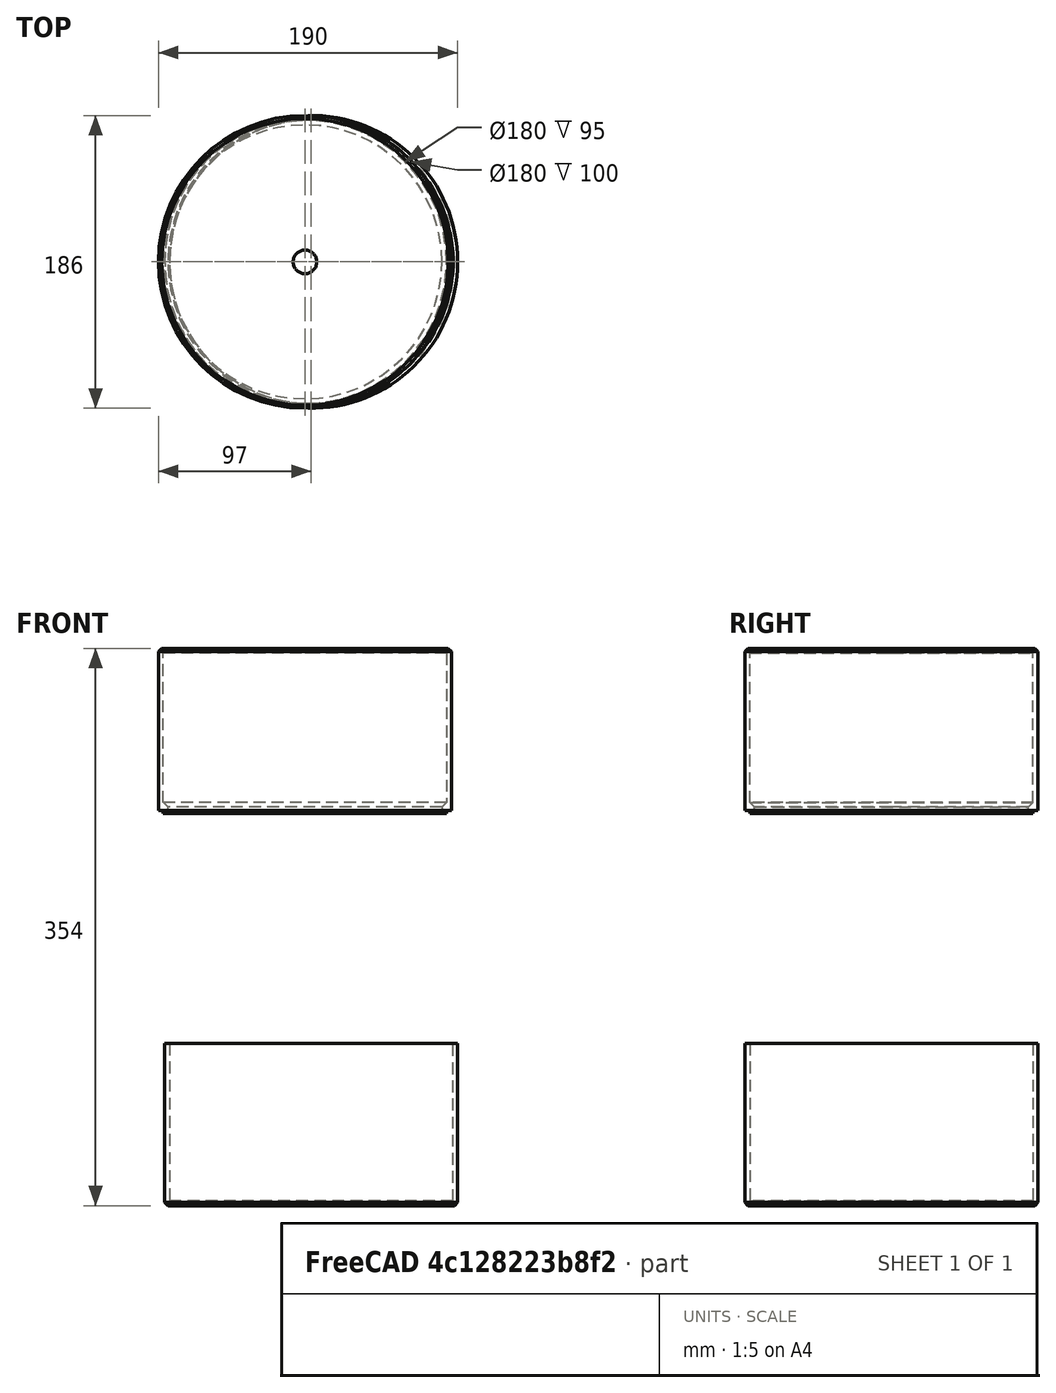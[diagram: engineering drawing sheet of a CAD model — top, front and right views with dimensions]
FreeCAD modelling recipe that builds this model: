
FCSTD DOCUMENT  (FreeCAD 1.0R39285 (Git))
Label: CanHalves
License: All rights reserved
LicenseURL: http://en.wikipedia.org/wiki/All_rights_reserved
objects: PartDesign::Chamfer×3, App::Link×2, App::FeaturePython×2, Sketcher::SketchObject×2, PartDesign::Body×2, PartDesign::AdditiveCylinder×1, PartDesign::Thickness×1, PartDesign::FeatureBase×1, PartDesign::Pad×1, Assembly::JointGroup×1, Assembly::AssemblyObject×1, PartDesign::Pocket×1
note: 29 computed .brp shape members not serialized (recipe doc carries the construction recipe); baked Part::Feature solids carry a one-line shape summary decoded from their .brp

FEATURE [PartDesign::AdditiveCylinder] Cylinder
  Angle = 360
  AttacherType = Attacher::AttachEngine3D
  Dimensions_Diameter = 180
  Dimensions_Height = 200
  Dimensions_Thickness = 3
  FirstAngle = 0
  Height = 103
  Radius = 93
  SecondAngle = 0
  Suppressed = false
  expr: Height = Dimensions_Height / 2 + Dimensions_Thickness
  expr: Radius = Dimensions_Diameter / 2 + Dimensions_Thickness
FEATURE [PartDesign::Thickness] Thickness
  Base = -> Cylinder [Face3]
  BaseFeature = -> Cylinder
  Intersection = false
  Join = 0
  Mode = 0
  Reversed = true
  SupportTransform = false
  Suppressed = false
  Value = 3
  expr: Value = <<Cylinder>>.Dimensions_Thickness
FEATURE [PartDesign::FeatureBase] Clone
  BaseFeature = -> Thickness
  Suppressed = false
FEATURE [App::Link] Bottom_Body  label="Bottom Body001"
  LinkedObject = -> Body
FEATURE [App::FeaturePython] GroundedJoint  # Assembly grounded joint (typed FeaturePython)
  ObjectToGround = -> Bottom_Body
FEATURE [App::Link] Top_Body  label="Top Body001"
  LinkPlacement = pos=(0,0,238.657) rot=(1,0,0;3.14159rad)
  LinkedObject = -> Body001
  Placement = pos=(0,0,238.657) rot=(1,0,0;3.14159rad)
FEATURE [Sketcher::SketchObject] Sketch
  ArcFitTolerance = 1e-06
  AttachmentOffset = pos=(0,0,-5) rot=(0,0,1;0rad)
  AttachmentSupport = -> [Clone]
  ExternalGeometry = -> [Clone]
  FullyConstrained = true
  MakeInternals = false
  MapMode = 5
  Placement = pos=(0,0,98) rot=(0,0,1;0rad)
  expr: Constraints[3] = <<Cylinder>>.Dimensions_Thickness
  sketch-geometry (2):
    g0: Circle CenterX=0 CenterY=0 CenterZ=0 NormalX=0 NormalY=0 NormalZ=1 AngleXU=0 Radius=90
    g1: Circle CenterX=0 CenterY=0 CenterZ=0 NormalX=0 NormalY=0 NormalZ=1 AngleXU=0 Radius=87
  constraints (4):
    c: Coincident(g0,g-1)
    c: Equal(g0,g-3)
    c: Coincident(g1,g0)
    c: Distance(g1,g0) = 3
FEATURE [PartDesign::Pad] Pad
  BaseFeature = -> Clone
  Direction = (0,0,1)
  Length = 7
  Length2 = 10
  Profile = -> Sketch
  ReferenceAxis = -> Sketch [N_Axis]
  Suppressed = false
  Type = 0
FEATURE [PartDesign::Chamfer] Chamfer
  Angle = 45
  Base = -> Pad [Edge2]
  BaseFeature = -> Pad
  ChamferType = 0
  FlipDirection = false
  Size = 2
  Size2 = 1
  SupportTransform = false
  Suppressed = false
  UseAllEdges = false
FEATURE [PartDesign::Chamfer] Chamfer001
  Angle = 45
  Base = -> Thickness [Edge2]
  BaseFeature = -> Thickness
  ChamferType = 0
  FlipDirection = false
  Size = 2
  Size2 = 1
  SupportTransform = false
  Suppressed = false
  UseAllEdges = false
FEATURE [PartDesign::Body] Body  label="Bottom Body"
  AllowCompound = false
  Group = -> [Cylinder,Thickness,Chamfer001]
  Origin = -> Origin
  Tip = -> Chamfer001
FEATURE [PartDesign::Chamfer] Chamfer002
  Angle = 45
  Base = -> Chamfer [Edge11]
  BaseFeature = -> Chamfer
  ChamferType = 0
  FlipDirection = false
  Size = 2.9
  Size2 = 1
  SupportTransform = false
  Suppressed = false
  UseAllEdges = false
  expr: Size = <<Cylinder>>.Dimensions_Thickness - 0.1 mm
FEATURE [App::FeaturePython] Joint  label="Slider"  # Assembly joint (typed FeaturePython)
  Activated = true
  AngleMax = 0
  AngleMin = 0
  Detach1 = false
  Detach2 = false
  Distance = 0
  Distance2 = 0
  EnableAngleMax = false
  EnableAngleMin = false
  EnableLengthMax = false
  EnableLengthMin = true
  JointType = 3 (Slider)
  LengthMax = 0
  LengthMin = 0
  Placement1 = pos=(0,0,103) rot=(0,0,1;0rad)
  Placement2 = pos=(0,0,103) rot=(0,0,1;0rad)
  Reference1 = -> Assembly [Top_Body.Chamfer002.Edge12,Top_Body.Chamfer002.Edge12]
  Reference2 = -> Assembly [Bottom_Body.Chamfer001.Edge3,Bottom_Body.Chamfer001.Edge3]
FEATURE [Assembly::JointGroup] Joints
  Group = -> [GroundedJoint,Joint]
FEATURE [Assembly::AssemblyObject] Assembly
  Group = -> [Joints,Bottom_Body,GroundedJoint,Top_Body,Joint]
  Origin = -> Origin002
  Type = Assembly
FEATURE [Sketcher::SketchObject] Sketch001
  ArcFitTolerance = 1e-06
  AttachmentSupport = -> [Chamfer002]
  FullyConstrained = true
  MakeInternals = false
  MapMode = 5
  Placement = pos=(0,0,0) rot=(1,0,0;3.14159rad)
  sketch-geometry (1):
    g0: Circle CenterX=0 CenterY=0 CenterZ=0 NormalX=0 NormalY=0 NormalZ=1 AngleXU=0 Radius=7.5
  constraints (2):
    c: Diameter(g0) = 15
    c: Coincident(g0,g-1)
FEATURE [PartDesign::Pocket] Pocket
  BaseFeature = -> Chamfer002
  Direction = (0,0,1)
  Length = 5
  Length2 = 5
  Profile = -> Sketch001
  ReferenceAxis = -> Sketch001 [N_Axis]
  Suppressed = false
  Type = 1
FEATURE [PartDesign::Body] Body001  label="Top Body"
  AllowCompound = false
  Group = -> [Clone,Sketch,Pad,Chamfer,Chamfer002,Sketch001,Pocket]
  Origin = -> Origin001
  Placement = pos=(-4,4.34e-14,354) rot=(1,0,0;3.14159rad)
  Tip = -> Pocket
